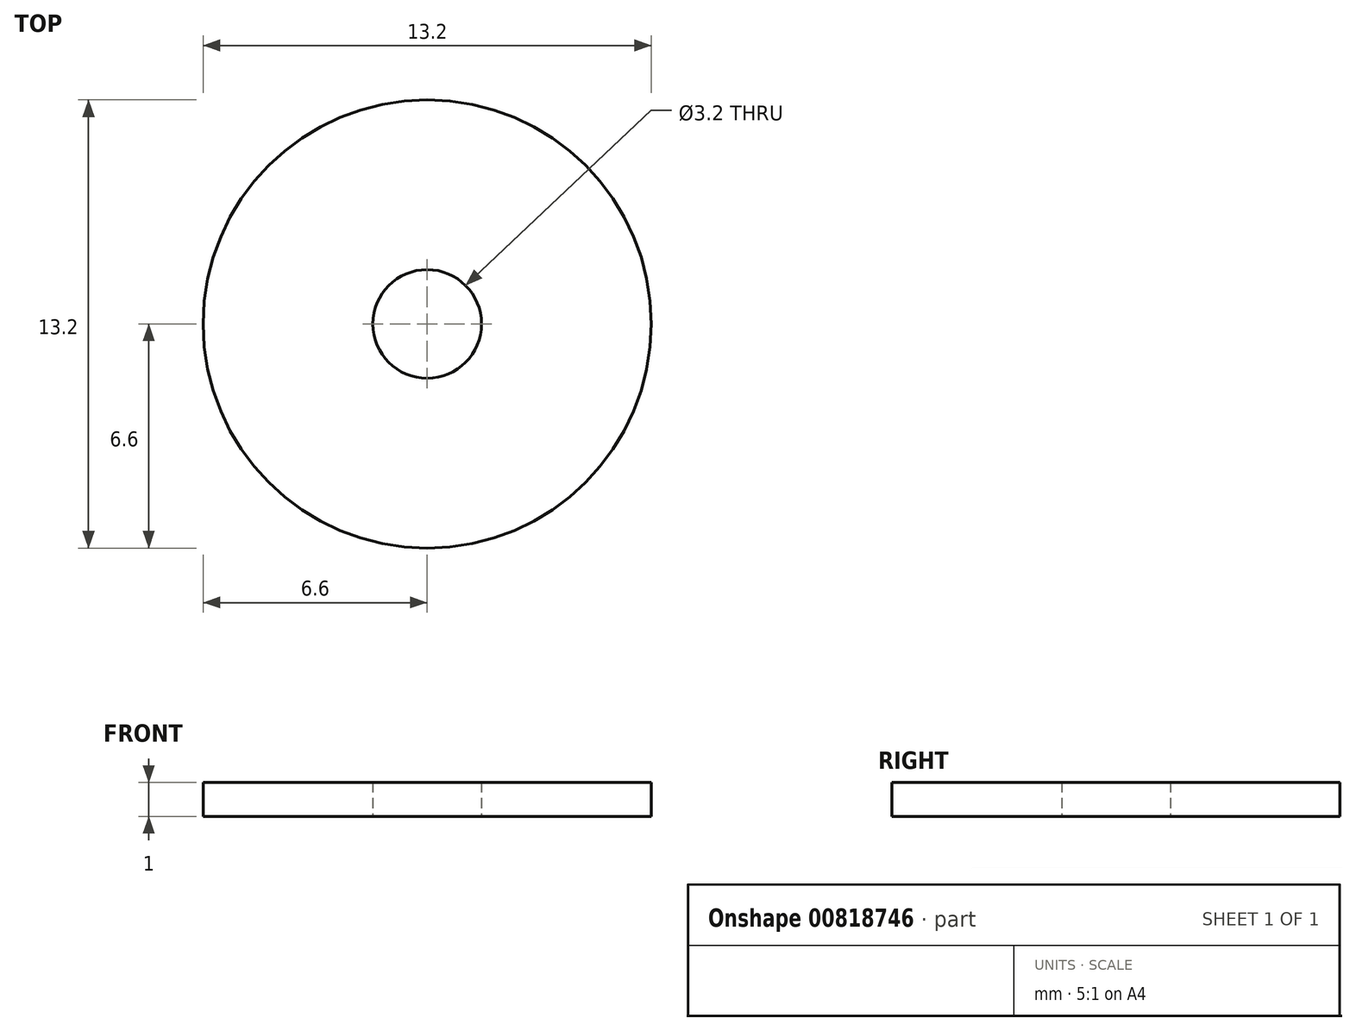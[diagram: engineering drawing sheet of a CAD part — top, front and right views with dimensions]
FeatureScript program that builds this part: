
annotation { "Feature Type Name" : "Feature", "Feature Type Description" : "" }
export const myFeature = defineFeature(function(context is Context, id is Id, definition is map)
    precondition{}
    {
        {
            var Q0;
            Q0=qCreatedBy(makeId("Top.planeOp"),FACE);
            var sketch = newSketch(context, id + "F0", { "sketchPlane" : qUnion([Q0])});
            skCircle(sketch, "E0", {"center": v(0, 0) * mm, "radius": 6.6 * mm});
            skCircle(sketch, "E1", {"center": v(0, 0) * mm, "radius": 1.6 * mm});
            skSolve(sketch);
        }
        {
            var Q0;
            Q0=makeQuery(id+"F0.imprint","IMPRINT",FACE,{"disambiguationData":[TD([[makeQuery(id+"F0.imprint","IMPRINT",EDGE,{"derivedFrom":sQuery(id+"F0.wireOp",EDGE,"E0")}),1.0]])]});
            extrude(context, id + "F1", {"entities" : qUnion([Q0]), "depth" : 1 * mm, "offsetDistance" : 25 * mm});
        }
    });
